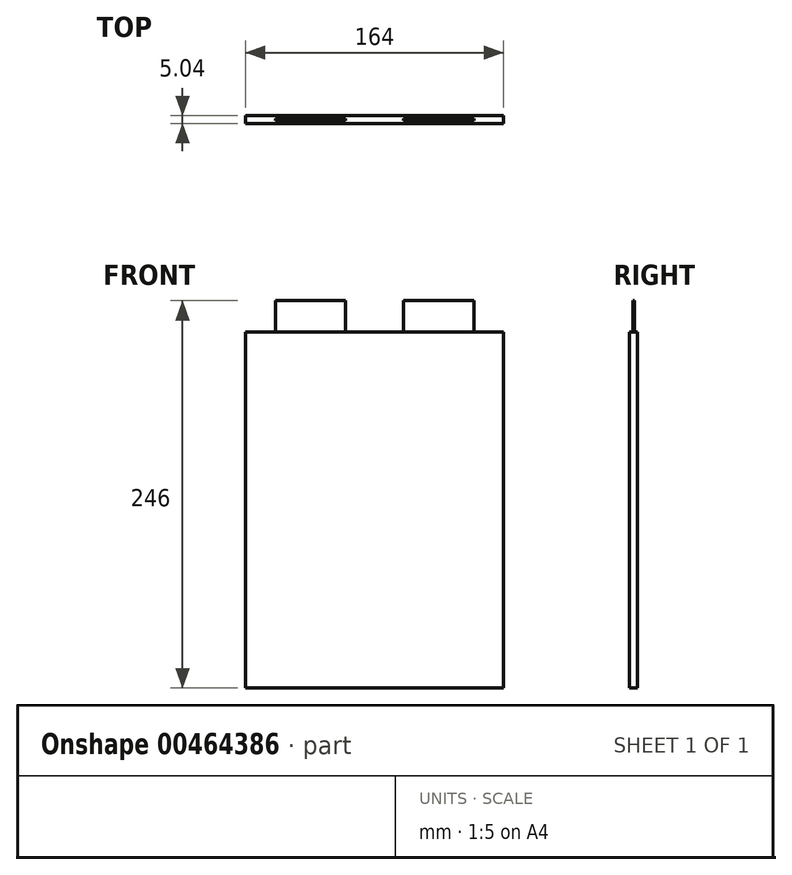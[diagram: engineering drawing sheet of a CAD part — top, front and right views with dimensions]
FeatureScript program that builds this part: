
annotation { "Feature Type Name" : "Feature", "Feature Type Description" : "" }
export const myFeature = defineFeature(function(context is Context, id is Id, definition is map)
    precondition{}
    {
        {
            var Q0;
            Q0=qCreatedBy(makeId("Front.planeOp"),FACE);
            var sketch = newSketch(context, id + "F0", { "sketchPlane" : qUnion([Q0])});
            skLineSegment(sketch, "E0.bottom", {"start": v(-82, 113) * mm, "end": v(82, 113) * mm});
            skLineSegment(sketch, "E0.top", {"start": v(-82, -113) * mm, "end": v(82, -113) * mm});
            skLineSegment(sketch, "E0.left", {"start": v(-82, 113) * mm, "end": v(-82, -113) * mm});
            skLineSegment(sketch, "E0.right", {"start": v(82, 113) * mm, "end": v(82, -113) * mm});
            skPoint(sketch, "E0.middle", {"position": v(0, 0) * mm});
            skSolve(sketch);
        }
        {
            var Q0;
            Q0=makeQuery(id+"F0.imprint","IMPRINT",FACE,{"disambiguationData":[TD([[makeQuery(id+"F0.imprint","IMPRINT",EDGE,{"derivedFrom":sQuery(id+"F0.wireOp",EDGE,"E0.bottom")}),-1.0]])]});
            extrude(context, id + "F1", {"entities" : qUnion([Q0]), "endBound" : BoundingType.SYMMETRIC, "depth" : 5.05 * mm});
        }
        {
            var Q0;
            Q0=makeQuery(id+"F0.imprint","IMPRINT",FACE,{"disambiguationData":[TD([[makeQuery(id+"F0.imprint","IMPRINT",EDGE,{"derivedFrom":sQuery(id+"F0.wireOp",EDGE,"E0.bottom")}),-1.0]])]});
            var sketch = newSketch(context, id + "F2", { "sketchPlane" : qUnion([Q0])});
            skLineSegment(sketch, "E1.bottom", {"start": v(-63, 133) * mm, "end": v(-18.33, 133) * mm});
            skLineSegment(sketch, "E1.top", {"start": v(-63, 113) * mm, "end": v(-18.33, 113) * mm});
            skLineSegment(sketch, "E1.left", {"start": v(-63, 133) * mm, "end": v(-63, 113) * mm});
            skLineSegment(sketch, "E1.right", {"start": v(-18.33, 133) * mm, "end": v(-18.33, 113) * mm});
            skLineSegment(sketch, "E2.MirrorCS", {"start": v(63, 133) * mm, "end": v(18.33, 133) * mm});
            skLineSegment(sketch, "E3.MirrorCS", {"start": v(18.33, 133) * mm, "end": v(18.33, 113) * mm});
            skLineSegment(sketch, "E4.MirrorCS", {"start": v(63, 113) * mm, "end": v(18.33, 113) * mm});
            skLineSegment(sketch, "E5.MirrorCS", {"start": v(63, 133) * mm, "end": v(63, 113) * mm});
            skSolve(sketch);
        }
        {
            var Q0;
            Q0=makeQuery(id+"F2.imprint","IMPRINT",FACE,{"disambiguationData":[TD([[makeQuery(id+"F2.imprint","IMPRINT",EDGE,{"derivedFrom":sQuery(id+"F2.wireOp",EDGE,"E1.bottom")}),-1.0]])]});
            var Q1;
            Q1=makeQuery(id+"F2.imprint","IMPRINT",FACE,{"disambiguationData":[TD([[makeQuery(id+"F2.imprint","IMPRINT",EDGE,{"derivedFrom":sQuery(id+"F2.wireOp",EDGE,"E2.MirrorCS")}),1.0]])]});
            extrude(context, id + "F3", {"entities" : qUnion([Q0, Q1]), "operationType" : NewBodyOperationType.ADD, "endBound" : BoundingType.SYMMETRIC, "depth" : 1 * mm});
        }
    });
